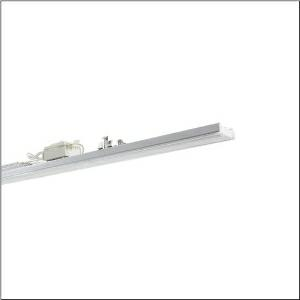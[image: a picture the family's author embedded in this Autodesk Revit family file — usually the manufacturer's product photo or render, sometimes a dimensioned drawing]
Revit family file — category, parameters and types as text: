
# Revit family: licross_r__21_recessed_ho_52tl1wdv4l2m_5148
name_source: partatom
category: Lighting Fixtures
units: mm (PartAtom-declared; Revit-internal decimal feet)

## family parameters
Cut with Voids When Loaded = No
Host = Face
Light Source = No
Part Type = Normal
Room Calculation Point = No
Round Connector Dimension = Use Diameter
Shared = No

## types (1)
- --- (1 x LED, 22780 lm, 125.6 W, 4000K)
    Apparent Load = 126 VA
    CIE Flux Codes = 73 94 99 100 100
    Color Rendering = 80
    Color Temperature = 4000K
    Default Elevation = 1800 mm
    Description = Licross® 21 Recessed HO, luminaire insert, of sheet steel, galvanised, coil coated, white, length: 2.250mm, width: 66mm, height: 67mm, LED rated luminous flux: 22.780lm, light colour: 840, control gear: DALI 2, with plug, 5-pole, with phase selection, mains connection: 220..240V, AC, 50/60Hz, rated input power: 126W, halogen-free wiring, primary optical cover: cover, of PMMA, light emission: direct distribution, primary light characteristic: symmetric, protection rating (complete): IP40, insulation class (complete): insulation class I (protective earthing), certification: CE, ENEC, VDE, UKCA, protection symbol: D if used in an environment without relevant dust loads with corresponding accessories, impact resistance: IK06, permissible ambient temperature for indoor applications: -40..+30°C, corresponds to IFS (International Featured Standards) requirements for safety and quality in the food industry, reducing of maximum allowable ambient temperature of 5°C with ceiling mounting, LABS conformity tested according to VDMA 24364:2018-05, packaging unit: 1 piece
    Height = 58 mm
    Lamp = 1 x LED
    Lamp Light Flux = 22780 lm
    Lamp Power = 125.6 W
    Lamp count = 1
    Length = 2250 mm
    Luminous efficacy = 181 lm/W
    Manufacturer = Siteco
    ModVariant = No
    Model = 52TL1WDV4L2M
    Mounting Place = Ceiling
    Mounting Type = Pendant
    Number of Poles = 1
    OnlyDefault = Yes
    Power Factor = 1
    Product Name = Licross® 21 Recessed HO
    Product group = luminaire insert
    ProductGroupID = 902
    Protection Class = Protection class I
    Protection Degree = IP 40
    RLX_Detail_Level = 1
    RLX_Emergency_Light_Flux = 0 lm
    RLX_Emergency_Type = 0
    RLX_Emergency_Type_DB = No
    RlxData = <blob elided: 29645 chars, md5=e409212e>
    Socket = socket
    Standby Power = 0 W
    System Light Flux = 22780 lm
    System Power = 126 W
    Type Comments = factory setting: luminous flux: 100 % | dim-lin: 254 | 489 mA
    Type Image = l_1296930.jpg
    URL = http://relux.com
    VarID = @adj_060140
    Voltage = 0 V
    Weight = 0.00 kg
    Width = 66 mm

## geometry (parser evidence)
native form markers: Blend x4, Sweep x10
no freeform markers — native parametric forms only
